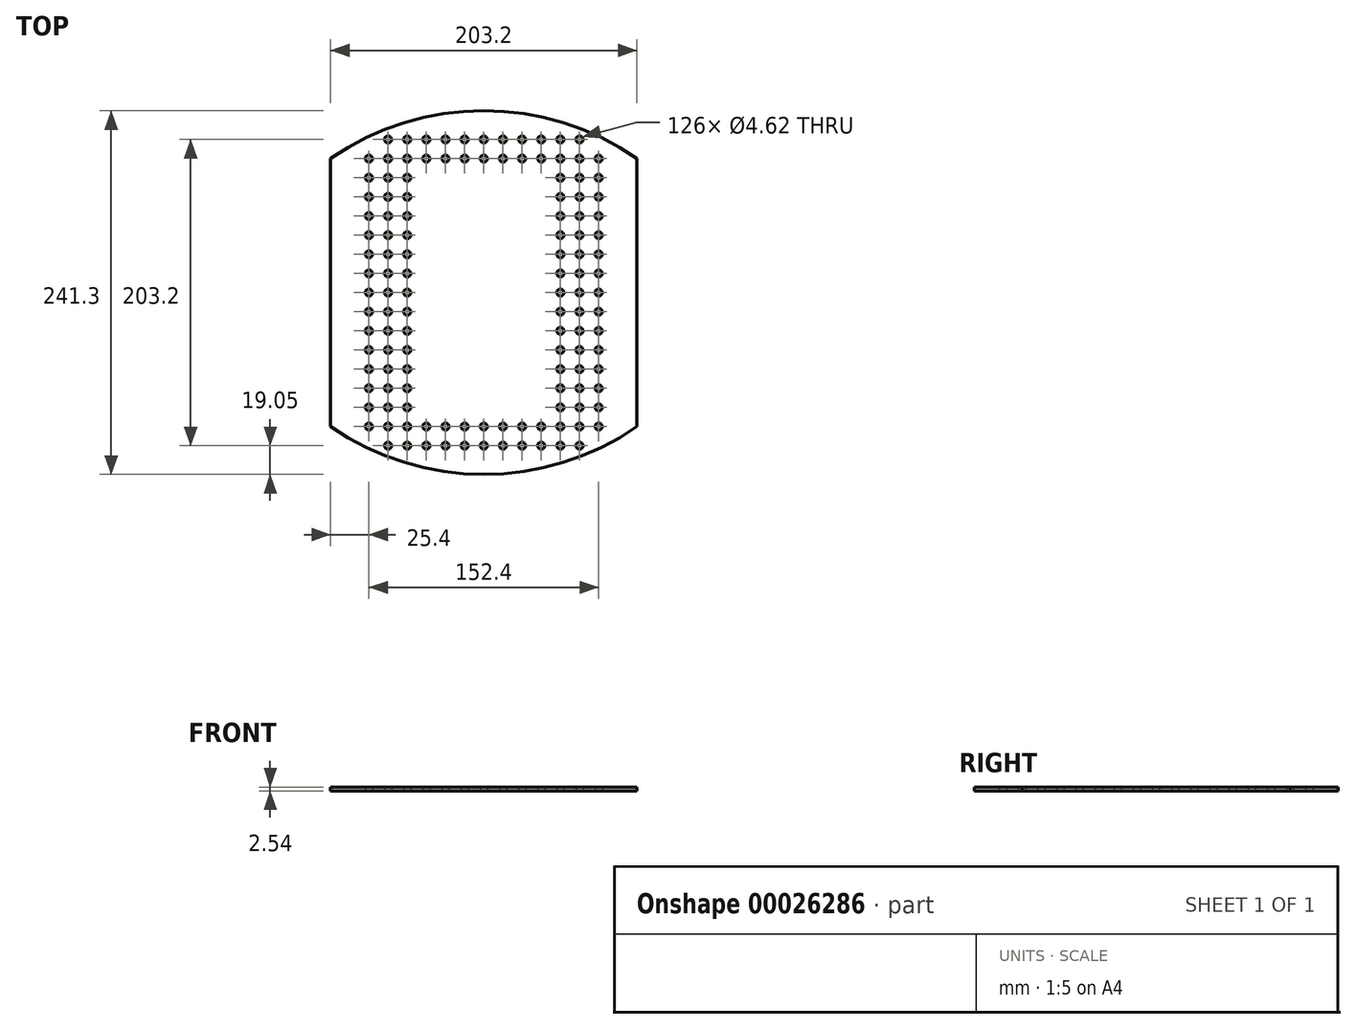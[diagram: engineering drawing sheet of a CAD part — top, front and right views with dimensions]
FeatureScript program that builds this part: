
annotation { "Feature Type Name" : "Feature", "Feature Type Description" : "" }
export const myFeature = defineFeature(function(context is Context, id is Id, definition is map)
    precondition{}
    {
        {
            var Q0;
            Q0=qCreatedBy(makeId("Top.planeOp"),FACE);
            var sketch = newSketch(context, id + "F0", { "sketchPlane" : qUnion([Q0])});
            skLineSegment(sketch, "E0", {"start": v(-101.6, 64.48) * mm, "end": v(-101.6, 88.9) * mm});
            skPoint(sketch, "E1.orphan", {"position": v(0, 120.65) * mm});
            skLineSegment(sketch, "E2.MirrorCS", {"start": v(-101.6, -88.9) * mm, "end": v(-101.6, -64.48) * mm});
            skLineSegment(sketch, "E3.MirrorCS", {"start": v(101.6, -88.9) * mm, "end": v(101.6, -64.48) * mm});
            skLineSegment(sketch, "E4.trimOffspring", {"start": v(-101.6, -64.48) * mm, "end": v(-101.6, -83.53) * mm});
            skPoint(sketch, "E5.orphan", {"position": v(101.6, 64.48) * mm});
            skLineSegment(sketch, "E6", {"start": v(101.6, 88.9) * mm, "end": v(101.6, 64.48) * mm});
            skPoint(sketch, "E7.MirrorCS.end.orphan", {"position": v(0, -120.65) * mm});
            skLineSegment(sketch, "E8.trimOffspring", {"start": v(7.61, 0) * mm, "end": v(7.62, 0) * mm, "construction": true});
            skPoint(sketch, "E9.orphan", {"position": v(-101.6, -88.9) * mm});
            skPoint(sketch, "E10.MirrorCS.start.orphan", {"position": v(101.6, -88.9) * mm});
            skArc(sketch, "E11", {"start": v(101.6, 88.9) * mm, "mid": v(0, 120.65) * mm, "end": v(-101.6, 88.9) * mm});
            skArc(sketch, "E12", {"start": v(-101.6, -88.9) * mm, "mid": v(0, -120.65) * mm, "end": v(101.6, -88.9) * mm});
            skCircle(sketch, "E13.0.7.0", {"center": v(0, 88.9) * mm, "radius": 2.31 * mm});
            skCircle(sketch, "E13.0.8.0", {"center": v(0, 101.6) * mm, "radius": 2.31 * mm});
            skCircle(sketch, "E13.1.7.0", {"center": v(12.7, 88.9) * mm, "radius": 2.31 * mm});
            skCircle(sketch, "E13.1.8.0", {"center": v(12.7, 101.6) * mm, "radius": 2.31 * mm});
            skCircle(sketch, "E13.2.7.0", {"center": v(25.4, 88.9) * mm, "radius": 2.31 * mm});
            skCircle(sketch, "E13.2.8.0", {"center": v(25.4, 101.6) * mm, "radius": 2.31 * mm});
            skCircle(sketch, "E13.3.7.0", {"center": v(38.1, 88.9) * mm, "radius": 2.31 * mm});
            skCircle(sketch, "E13.3.8.0", {"center": v(38.1, 101.6) * mm, "radius": 2.31 * mm});
            skCircle(sketch, "E13.4.0.0", {"center": v(50.8, 0) * mm, "radius": 2.31 * mm});
            skCircle(sketch, "E13.4.1.0", {"center": v(50.8, 12.7) * mm, "radius": 2.31 * mm});
            skCircle(sketch, "E13.4.2.0", {"center": v(50.8, 25.4) * mm, "radius": 2.31 * mm});
            skCircle(sketch, "E13.4.3.0", {"center": v(50.8, 38.1) * mm, "radius": 2.31 * mm});
            skCircle(sketch, "E13.4.4.0", {"center": v(50.8, 50.8) * mm, "radius": 2.31 * mm});
            skCircle(sketch, "E13.4.5.0", {"center": v(50.8, 63.5) * mm, "radius": 2.31 * mm});
            skCircle(sketch, "E13.4.6.0", {"center": v(50.8, 76.2) * mm, "radius": 2.31 * mm});
            skCircle(sketch, "E13.4.7.0", {"center": v(50.8, 88.9) * mm, "radius": 2.31 * mm});
            skCircle(sketch, "E13.4.8.0", {"center": v(50.8, 101.6) * mm, "radius": 2.31 * mm});
            skCircle(sketch, "E13.5.0.0", {"center": v(63.5, 0) * mm, "radius": 2.31 * mm});
            skCircle(sketch, "E13.5.1.0", {"center": v(63.5, 12.7) * mm, "radius": 2.31 * mm});
            skCircle(sketch, "E13.5.2.0", {"center": v(63.5, 25.4) * mm, "radius": 2.31 * mm});
            skCircle(sketch, "E13.5.3.0", {"center": v(63.5, 38.1) * mm, "radius": 2.31 * mm});
            skCircle(sketch, "E13.5.4.0", {"center": v(63.5, 50.8) * mm, "radius": 2.31 * mm});
            skCircle(sketch, "E13.5.5.0", {"center": v(63.5, 63.5) * mm, "radius": 2.31 * mm});
            skCircle(sketch, "E13.5.6.0", {"center": v(63.5, 76.2) * mm, "radius": 2.31 * mm});
            skCircle(sketch, "E13.5.7.0", {"center": v(63.5, 88.9) * mm, "radius": 2.31 * mm});
            skCircle(sketch, "E13.5.8.0", {"center": v(63.5, 101.6) * mm, "radius": 2.31 * mm});
            skCircle(sketch, "E13.6.0.0", {"center": v(76.2, 0) * mm, "radius": 2.31 * mm});
            skCircle(sketch, "E13.6.1.0", {"center": v(76.2, 12.7) * mm, "radius": 2.31 * mm});
            skCircle(sketch, "E13.6.2.0", {"center": v(76.2, 25.4) * mm, "radius": 2.31 * mm});
            skCircle(sketch, "E13.6.3.0", {"center": v(76.2, 38.1) * mm, "radius": 2.31 * mm});
            skCircle(sketch, "E13.6.4.0", {"center": v(76.2, 50.8) * mm, "radius": 2.31 * mm});
            skCircle(sketch, "E13.6.5.0", {"center": v(76.2, 63.5) * mm, "radius": 2.31 * mm});
            skCircle(sketch, "E13.6.6.0", {"center": v(76.2, 76.2) * mm, "radius": 2.31 * mm});
            skCircle(sketch, "E13.6.7.0", {"center": v(76.2, 88.9) * mm, "radius": 2.31 * mm});
            skCircle(sketch, "E14.MirrorC", {"center": v(-63.5, 63.5) * mm, "radius": 2.31 * mm});
            skCircle(sketch, "E15.MirrorC", {"center": v(-50.8, 88.9) * mm, "radius": 2.31 * mm});
            skCircle(sketch, "E16.MirrorC", {"center": v(-76.2, 0) * mm, "radius": 2.31 * mm});
            skCircle(sketch, "E17.MirrorC", {"center": v(-63.5, 0) * mm, "radius": 2.31 * mm});
            skCircle(sketch, "E18.MirrorC", {"center": v(-76.2, 50.8) * mm, "radius": 2.31 * mm});
            skCircle(sketch, "E19.MirrorC", {"center": v(-76.2, 63.5) * mm, "radius": 2.31 * mm});
            skCircle(sketch, "E20.MirrorC", {"center": v(-63.5, 25.4) * mm, "radius": 2.31 * mm});
            skCircle(sketch, "E21.MirrorC", {"center": v(-50.8, 0) * mm, "radius": 2.31 * mm});
            skCircle(sketch, "E22.MirrorC", {"center": v(-76.2, 88.9) * mm, "radius": 2.31 * mm});
            skCircle(sketch, "E23.MirrorC", {"center": v(-63.5, 88.9) * mm, "radius": 2.31 * mm});
            skCircle(sketch, "E24.MirrorC", {"center": v(-63.5, 101.6) * mm, "radius": 2.31 * mm});
            skCircle(sketch, "E25.MirrorC", {"center": v(-63.5, 76.2) * mm, "radius": 2.31 * mm});
            skCircle(sketch, "E26.MirrorC", {"center": v(-38.1, 101.6) * mm, "radius": 2.31 * mm});
            skCircle(sketch, "E27.MirrorC", {"center": v(-76.2, 25.4) * mm, "radius": 2.31 * mm});
            skCircle(sketch, "E28.MirrorC", {"center": v(-50.8, 38.1) * mm, "radius": 2.31 * mm});
            skCircle(sketch, "E29.MirrorC", {"center": v(-12.7, 88.9) * mm, "radius": 2.31 * mm});
            skCircle(sketch, "E30.MirrorC", {"center": v(-50.8, 101.6) * mm, "radius": 2.31 * mm});
            skCircle(sketch, "E31.MirrorC", {"center": v(-63.5, 38.1) * mm, "radius": 2.31 * mm});
            skCircle(sketch, "E32.MirrorC", {"center": v(-50.8, 63.5) * mm, "radius": 2.31 * mm});
            skCircle(sketch, "E33.MirrorC", {"center": v(-25.4, 88.9) * mm, "radius": 2.31 * mm});
            skCircle(sketch, "E34.MirrorC", {"center": v(-76.2, 38.1) * mm, "radius": 2.31 * mm});
            skCircle(sketch, "E35.MirrorC", {"center": v(-76.2, 76.2) * mm, "radius": 2.31 * mm});
            skCircle(sketch, "E36.MirrorC", {"center": v(-12.7, 101.6) * mm, "radius": 2.31 * mm});
            skCircle(sketch, "E37.MirrorC", {"center": v(-50.8, 50.8) * mm, "radius": 2.31 * mm});
            skCircle(sketch, "E38.MirrorC", {"center": v(-50.8, 25.4) * mm, "radius": 2.31 * mm});
            skCircle(sketch, "E39.MirrorC", {"center": v(-63.5, 50.8) * mm, "radius": 2.31 * mm});
            skCircle(sketch, "E40.MirrorC", {"center": v(-63.5, 12.7) * mm, "radius": 2.31 * mm});
            skCircle(sketch, "E41.MirrorC", {"center": v(-38.1, 88.9) * mm, "radius": 2.31 * mm});
            skCircle(sketch, "E42.MirrorC", {"center": v(-50.8, 76.2) * mm, "radius": 2.31 * mm});
            skCircle(sketch, "E43.MirrorC", {"center": v(-25.4, 101.6) * mm, "radius": 2.31 * mm});
            skCircle(sketch, "E44.MirrorC", {"center": v(-76.2, 12.7) * mm, "radius": 2.31 * mm});
            skCircle(sketch, "E45.MirrorC", {"center": v(-50.8, 12.7) * mm, "radius": 2.31 * mm});
            skCircle(sketch, "E46.MirrorC", {"center": v(63.5, -63.5) * mm, "radius": 2.31 * mm});
            skCircle(sketch, "E47.MirrorC", {"center": v(76.2, -38.1) * mm, "radius": 2.31 * mm});
            skCircle(sketch, "E48.MirrorC", {"center": v(-50.8, -76.2) * mm, "radius": 2.31 * mm});
            skCircle(sketch, "E49.MirrorC", {"center": v(63.5, -12.7) * mm, "radius": 2.31 * mm});
            skCircle(sketch, "E50.MirrorC", {"center": v(-50.8, -25.4) * mm, "radius": 2.31 * mm});
            skCircle(sketch, "E51.MirrorC", {"center": v(-50.8, -101.6) * mm, "radius": 2.31 * mm});
            skCircle(sketch, "E52.MirrorC", {"center": v(-76.2, -12.7) * mm, "radius": 2.31 * mm});
            skCircle(sketch, "E53.MirrorC", {"center": v(-63.5, -38.1) * mm, "radius": 2.31 * mm});
            skCircle(sketch, "E54.MirrorC", {"center": v(-38.1, -101.6) * mm, "radius": 2.31 * mm});
            skCircle(sketch, "E55.MirrorC", {"center": v(50.8, -12.7) * mm, "radius": 2.31 * mm});
            skCircle(sketch, "E56.MirrorC", {"center": v(76.2, -12.7) * mm, "radius": 2.31 * mm});
            skCircle(sketch, "E57.MirrorC", {"center": v(-50.8, -88.9) * mm, "radius": 2.31 * mm});
            skCircle(sketch, "E58.MirrorC", {"center": v(63.5, -76.2) * mm, "radius": 2.31 * mm});
            skCircle(sketch, "E59.MirrorC", {"center": v(0, -101.6) * mm, "radius": 2.31 * mm});
            skCircle(sketch, "E60.MirrorC", {"center": v(50.8, -88.9) * mm, "radius": 2.31 * mm});
            skCircle(sketch, "E61.MirrorC", {"center": v(12.7, -101.6) * mm, "radius": 2.31 * mm});
            skCircle(sketch, "E62.MirrorC", {"center": v(63.5, -25.4) * mm, "radius": 2.31 * mm});
            skCircle(sketch, "E63.MirrorC", {"center": v(76.2, -88.9) * mm, "radius": 2.31 * mm});
            skCircle(sketch, "E64.MirrorC", {"center": v(50.8, -63.5) * mm, "radius": 2.31 * mm});
            skCircle(sketch, "E65.MirrorC", {"center": v(0, -88.9) * mm, "radius": 2.31 * mm});
            skCircle(sketch, "E66.MirrorC", {"center": v(25.4, -88.9) * mm, "radius": 2.31 * mm});
            skCircle(sketch, "E67.MirrorC", {"center": v(63.5, -88.9) * mm, "radius": 2.31 * mm});
            skCircle(sketch, "E68.MirrorC", {"center": v(-50.8, -38.1) * mm, "radius": 2.31 * mm});
            skCircle(sketch, "E69.MirrorC", {"center": v(76.2, -25.4) * mm, "radius": 2.31 * mm});
            skCircle(sketch, "E70.MirrorC", {"center": v(50.8, -76.2) * mm, "radius": 2.31 * mm});
            skCircle(sketch, "E71.MirrorC", {"center": v(25.4, -101.6) * mm, "radius": 2.31 * mm});
            skCircle(sketch, "E72.MirrorC", {"center": v(-76.2, -88.9) * mm, "radius": 2.31 * mm});
            skCircle(sketch, "E73.MirrorC", {"center": v(-63.5, -12.7) * mm, "radius": 2.31 * mm});
            skCircle(sketch, "E74.MirrorC", {"center": v(76.2, -76.2) * mm, "radius": 2.31 * mm});
            skCircle(sketch, "E75.MirrorC", {"center": v(-76.2, -76.2) * mm, "radius": 2.31 * mm});
            skCircle(sketch, "E76.MirrorC", {"center": v(-50.8, -63.5) * mm, "radius": 2.31 * mm});
            skCircle(sketch, "E77.MirrorC", {"center": v(-50.8, -12.7) * mm, "radius": 2.31 * mm});
            skCircle(sketch, "E78.MirrorC", {"center": v(-76.2, -63.5) * mm, "radius": 2.31 * mm});
            skCircle(sketch, "E79.MirrorC", {"center": v(-38.1, -88.9) * mm, "radius": 2.31 * mm});
            skCircle(sketch, "E80.MirrorC", {"center": v(-76.2, -38.1) * mm, "radius": 2.31 * mm});
            skCircle(sketch, "E81.MirrorC", {"center": v(-25.4, -88.9) * mm, "radius": 2.31 * mm});
            skCircle(sketch, "E82.MirrorC", {"center": v(50.8, -38.1) * mm, "radius": 2.31 * mm});
            skCircle(sketch, "E83.MirrorC", {"center": v(-76.2, -25.4) * mm, "radius": 2.31 * mm});
            skCircle(sketch, "E84.MirrorC", {"center": v(12.7, -88.9) * mm, "radius": 2.31 * mm});
            skCircle(sketch, "E85.MirrorC", {"center": v(63.5, -38.1) * mm, "radius": 2.31 * mm});
            skCircle(sketch, "E86.MirrorC", {"center": v(76.2, -63.5) * mm, "radius": 2.31 * mm});
            skCircle(sketch, "E87.MirrorC", {"center": v(50.8, -25.4) * mm, "radius": 2.31 * mm});
            skCircle(sketch, "E88.MirrorC", {"center": v(-63.5, -88.9) * mm, "radius": 2.31 * mm});
            skCircle(sketch, "E89.MirrorC", {"center": v(76.2, -50.8) * mm, "radius": 2.31 * mm});
            skCircle(sketch, "E90.MirrorC", {"center": v(-63.5, -76.2) * mm, "radius": 2.31 * mm});
            skCircle(sketch, "E91.MirrorC", {"center": v(63.5, -101.6) * mm, "radius": 2.31 * mm});
            skCircle(sketch, "E92.MirrorC", {"center": v(-63.5, -63.5) * mm, "radius": 2.31 * mm});
            skCircle(sketch, "E93.MirrorC", {"center": v(38.1, -101.6) * mm, "radius": 2.31 * mm});
            skCircle(sketch, "E94.MirrorC", {"center": v(-76.2, -50.8) * mm, "radius": 2.31 * mm});
            skCircle(sketch, "E95.MirrorC", {"center": v(-12.7, -101.6) * mm, "radius": 2.31 * mm});
            skCircle(sketch, "E96.MirrorC", {"center": v(63.5, -50.8) * mm, "radius": 2.31 * mm});
            skCircle(sketch, "E97.MirrorC", {"center": v(38.1, -88.9) * mm, "radius": 2.31 * mm});
            skCircle(sketch, "E98.MirrorC", {"center": v(50.8, -50.8) * mm, "radius": 2.31 * mm});
            skCircle(sketch, "E99.MirrorC", {"center": v(-12.7, -88.9) * mm, "radius": 2.31 * mm});
            skCircle(sketch, "E100.MirrorC", {"center": v(-50.8, -50.8) * mm, "radius": 2.31 * mm});
            skCircle(sketch, "E101.MirrorC", {"center": v(50.8, -101.6) * mm, "radius": 2.31 * mm});
            skCircle(sketch, "E102.MirrorC", {"center": v(-25.4, -101.6) * mm, "radius": 2.31 * mm});
            skCircle(sketch, "E103.MirrorC", {"center": v(-63.5, -101.6) * mm, "radius": 2.31 * mm});
            skCircle(sketch, "E104.MirrorC", {"center": v(-63.5, -25.4) * mm, "radius": 2.31 * mm});
            skCircle(sketch, "E105.MirrorC", {"center": v(-63.5, -50.8) * mm, "radius": 2.31 * mm});
            skLineSegment(sketch, "E106", {"start": v(-101.6, 64.48) * mm, "end": v(-101.6, -64.48) * mm});
            skLineSegment(sketch, "E107", {"start": v(101.6, 64.48) * mm, "end": v(101.6, -64.48) * mm});
            skPoint(sketch, "E108.bottom.end.orphan", {"position": v(-88.9, 64.48) * mm});
            skPoint(sketch, "E108.top.end.orphan", {"position": v(-88.9, -64.48) * mm});
            skPoint(sketch, "E109.MirrorCS.end.orphan", {"position": v(88.9, 64.48) * mm});
            skPoint(sketch, "E110.MirrorCS.end.orphan", {"position": v(88.9, -64.48) * mm});
            skPoint(sketch, "E111.MirrorCS.start.orphan", {"position": v(101.6, -64.48) * mm});
            skSolve(sketch);
        }
        {
            var Q0;
            Q0=makeQuery(id+"F0.imprint","IMPRINT",FACE,{"disambiguationData":[TD([[makeQuery(id+"F0.imprint","IMPRINT",EDGE,{"derivedFrom":sQuery(id+"F0.wireOp",EDGE,"E0")}),-1.0]])]});
            extrude(context, id + "F1", {"entities" : qUnion([Q0]), "depth" : 2.54 * mm});
        }
    });
